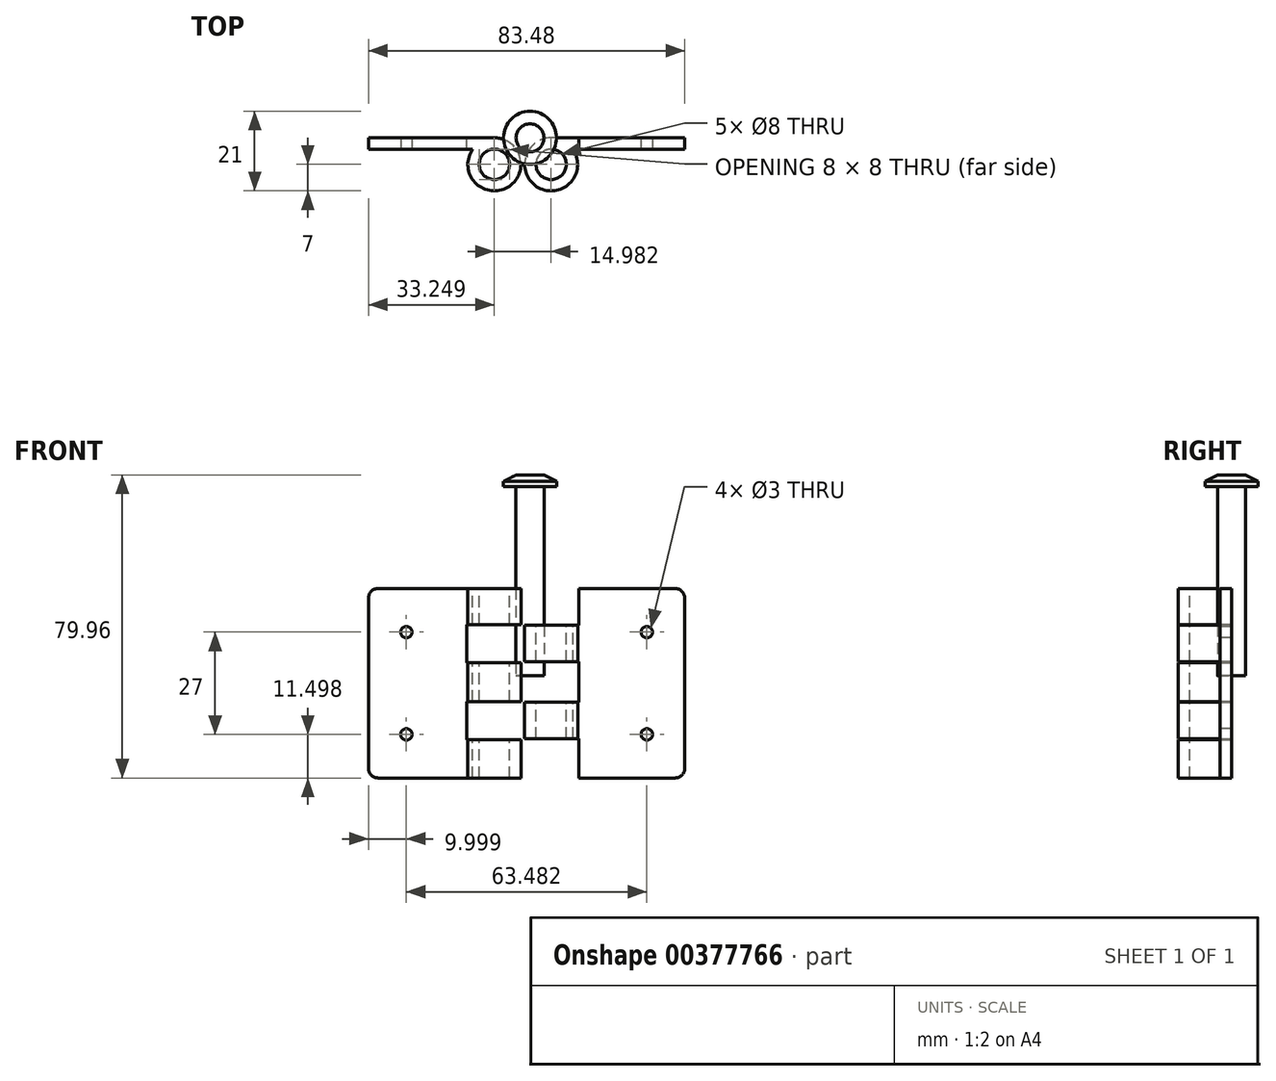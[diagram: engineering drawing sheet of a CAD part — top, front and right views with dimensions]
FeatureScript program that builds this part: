
annotation { "Feature Type Name" : "Feature", "Feature Type Description" : "" }
export const myFeature = defineFeature(function(context is Context, id is Id, definition is map)
    precondition{}
    {
        {
            var Q0;
            Q0=qCreatedBy(makeId("Front.planeOp"),FACE);
            var sketch = newSketch(context, id + "F0", { "sketchPlane" : qUnion([Q0])});
            skLineSegment(sketch, "E0.bottom", {"start": v(-44.61, 37.23) * mm, "end": v(-11.36, 37.23) * mm});
            skLineSegment(sketch, "E0.top", {"start": v(-44.61, -12.77) * mm, "end": v(-11.36, -12.77) * mm});
            skLineSegment(sketch, "E0.left", {"start": v(-44.61, 37.23) * mm, "end": v(-44.61, -12.77) * mm});
            skLineSegment(sketch, "E0.right", {"start": v(-11.36, 37.23) * mm, "end": v(-11.36, -12.77) * mm});
            skSolve(sketch);
        }
        {
            var Q0;
            Q0=qSketchRegion(id+"F0",true);
            extrude(context, id + "F1", {"entities" : qUnion([Q0]), "depth" : 3 * mm});
        }
        {
            var Q0;
            Q0=makeQuery(id+"F1.opExtrude","SWEPT_FACE",FACE,{"disambiguationData":[OSD([sQuery(id+"F0.wireOp",EDGE,"E0.bottom")])]});
            var sketch = newSketch(context, id + "F2", { "sketchPlane" : qUnion([Q0])});
            skCircle(sketch, "E1", {"center": v(-11.36, -7) * mm, "radius": 7 * mm});
            skCircle(sketch, "E2", {"center": v(-11.36, -7) * mm, "radius": 4 * mm});
            skSolve(sketch);
        }
        {
            var Q0;
            {var subQ5=sQuery(id+"F2.wireOp",EDGE,"E2");Q0=makeQuery(id+"F2.imprint","IMPRINT",FACE,{"disambiguationData":[TD([[makeQuery(id+"F2.imprint","IMPRINT",EDGE,{"derivedFrom":subQ5}),-1.0]])]});}
            var Q1;
            {var subQ1=sQuery(id+"F0.wireOp",EDGE,"E0.bottom");var subQ2=makeQuery(id+"F1.opExtrude","SWEPT_EDGE",EDGE,{"disambiguationData":[OSD([subQ1,sQuery(id+"F0.wireOp",EDGE,"E0.right")])]});Q1=makeQuery(id+"F2.imprint","IMPRINT",FACE,{"disambiguationData":[TD([[makeQuery(id+"F2.imprint","IMPRINT",EDGE,{"derivedFrom":subQ2}),1.0]])]});}
            var Q2;
            Q2=makeQuery(id+"F1.opExtrude","SWEPT_FACE",FACE,{"disambiguationData":[OSD([sQuery(id+"F0.wireOp",EDGE,"E0.top")])]});
            extrude(context, id + "F3", {"entities" : qUnion([Q0, Q1]), "operationType" : NewBodyOperationType.ADD, "endBound" : BoundingType.UP_TO_SURFACE, "oppositeDirection" : true, "endBoundEntityFace" : qUnion([Q2]), "depth" : 25.4 * mm});
        }
        {
            var Q0;
            Q0=makeQuery(id+"F1.opExtrude","CAP_FACE",FACE,{"disambiguationData":[OSD([sQuery(id+"F0.wireOp",EDGE,"E0.bottom"),sQuery(id+"F0.wireOp",EDGE,"E0.top"),sQuery(id+"F0.wireOp",EDGE,"E0.left"),sQuery(id+"F0.wireOp",EDGE,"E0.right")])],"isStart":false});
            var sketch = newSketch(context, id + "F4", { "sketchPlane" : qUnion([Q0])});
            skLineSegment(sketch, "E3", {"start": v(-34.61, 37.23) * mm, "end": v(-34.61, -12.77) * mm, "construction": true});
            skCircle(sketch, "E4", {"center": v(-34.61, 25.73) * mm, "radius": 1.5 * mm});
            skCircle(sketch, "E5", {"center": v(-34.61, -1.27) * mm, "radius": 1.5 * mm});
            skSolve(sketch);
        }
        {
            var Q0;
            Q0=makeQuery(id+"F1.opExtrude","SWEPT_EDGE",EDGE,{"disambiguationData":[OSD([sQuery(id+"F0.wireOp",EDGE,"E0.bottom"),sQuery(id+"F0.wireOp",EDGE,"E0.left")])]});
            var Q1;
            Q1=makeQuery(id+"F1.opExtrude","SWEPT_EDGE",EDGE,{"disambiguationData":[OSD([sQuery(id+"F0.wireOp",EDGE,"E0.top"),sQuery(id+"F0.wireOp",EDGE,"E0.left")])]});
            fillet(context, id + "F5", {"entities" : qUnion([Q0, Q1]), "radius" : 2.54 * mm, "tangentPropagation" : true, "allowEdgeOverflow" : false});
        }
        {
            var Q0;
            Q0=makeQuery(id+"F0.imprint","IMPRINT",FACE,{"disambiguationData":[TD([[makeQuery(id+"F0.imprint","IMPRINT",EDGE,{"derivedFrom":sQuery(id+"F0.wireOp",EDGE,"E0.bottom")}),-1.0]])]});
            var sketch = newSketch(context, id + "F6", { "sketchPlane" : qUnion([Q0])});
            skLineSegment(sketch, "E6", {"start": v(-18.61, -2.61) * mm, "end": v(-4.11, -2.61) * mm});
            skLineSegment(sketch, "E7", {"start": v(-4.11, -2.61) * mm, "end": v(-4.11, 7.39) * mm});
            skLineSegment(sketch, "E8", {"start": v(-4.11, 7.39) * mm, "end": v(-18.61, 7.39) * mm});
            skLineSegment(sketch, "E9", {"start": v(-18.61, 7.39) * mm, "end": v(-18.61, -2.61) * mm});
            skLineSegment(sketch, "E10", {"start": v(-18.61, 17.7) * mm, "end": v(-4.11, 17.7) * mm});
            skLineSegment(sketch, "E11", {"start": v(-4.11, 17.7) * mm, "end": v(-4.11, 27.7) * mm});
            skLineSegment(sketch, "E12", {"start": v(-4.11, 27.7) * mm, "end": v(-18.61, 27.7) * mm});
            skLineSegment(sketch, "E13", {"start": v(-18.61, 27.7) * mm, "end": v(-18.61, 17.7) * mm});
            skPoint(sketch, "E14", {"position": v(-11.36, -2.61) * mm});
            skLineSegment(sketch, "E15", {"start": v(-11.36, 27.7) * mm, "end": v(-11.36, 37.23) * mm});
            skLineSegment(sketch, "E16", {"start": v(-11.36, 17.7) * mm, "end": v(-11.36, 7.39) * mm});
            skLineSegment(sketch, "E17", {"start": v(-11.36, -2.61) * mm, "end": v(-11.36, -12.77) * mm});
            skLineSegment(sketch, "E18", {"start": v(-4.11, 17.7) * mm, "end": v(-4.11, 7.39) * mm});
            skLineSegment(sketch, "E19", {"start": v(-18.61, 7.39) * mm, "end": v(-18.61, 17.7) * mm});
            skLineSegment(sketch, "E20", {"start": v(-18.61, 27.7) * mm, "end": v(-18.61, 37.23) * mm});
            skLineSegment(sketch, "E21", {"start": v(-18.61, 37.23) * mm, "end": v(-4.11, 37.23) * mm});
            skLineSegment(sketch, "E22", {"start": v(-4.11, 37.23) * mm, "end": v(-4.11, 27.7) * mm});
            skLineSegment(sketch, "E23", {"start": v(-4.11, -2.61) * mm, "end": v(-4.11, -12.77) * mm});
            skLineSegment(sketch, "E24", {"start": v(-4.11, -12.77) * mm, "end": v(-18.61, -12.77) * mm});
            skLineSegment(sketch, "E25", {"start": v(-18.61, -12.77) * mm, "end": v(-18.61, -2.61) * mm});
            skSolve(sketch);
        }
        {
            var Q0;
            {var subQ0=sQuery(id+"F6.wireOp",EDGE,"E13");Q0=makeQuery(id+"F6.imprint","IMPRINT",FACE,{"disambiguationData":[TD([[makeQuery(id+"F6.imprint","IMPRINT",EDGE,{"derivedFrom":subQ0}),1.0]])]});}
            var Q1;
            {var subQ0=sQuery(id+"F6.wireOp",EDGE,"E11");Q1=makeQuery(id+"F6.imprint","IMPRINT",FACE,{"disambiguationData":[TD([[makeQuery(id+"F6.imprint","IMPRINT",EDGE,{"derivedFrom":subQ0}),1.0]])]});}
            var Q2;
            {var subQ0=sQuery(id+"F6.wireOp",EDGE,"E9");Q2=makeQuery(id+"F6.imprint","IMPRINT",FACE,{"disambiguationData":[TD([[makeQuery(id+"F6.imprint","IMPRINT",EDGE,{"derivedFrom":subQ0}),1.0]])]});}
            var Q3;
            {var subQ0=sQuery(id+"F6.wireOp",EDGE,"E7");Q3=makeQuery(id+"F6.imprint","IMPRINT",FACE,{"disambiguationData":[TD([[makeQuery(id+"F6.imprint","IMPRINT",EDGE,{"derivedFrom":subQ0}),1.0]])]});}
            extrude(context, id + "F7", {"entities" : qUnion([Q0, Q1, Q2, Q3]), "operationType" : NewBodyOperationType.REMOVE, "depth" : 25.4 * mm});
        }
        {
            var Q0;
            Q0=qCreatedBy(makeId("Front.planeOp"),FACE);
            var sketch = newSketch(context, id + "F8", { "sketchPlane" : qUnion([Q0])});
            skLineSegment(sketch, "E26.bottom", {"start": v(3.62, 37.23) * mm, "end": v(38.87, 37.23) * mm});
            skLineSegment(sketch, "E26.top", {"start": v(3.62, -12.77) * mm, "end": v(38.87, -12.77) * mm});
            skLineSegment(sketch, "E26.left", {"start": v(3.62, 37.23) * mm, "end": v(3.62, -12.77) * mm});
            skLineSegment(sketch, "E26.right", {"start": v(38.87, 37.23) * mm, "end": v(38.87, -12.77) * mm});
            skSolve(sketch);
        }
        {
            var Q0;
            Q0=qSketchRegion(id+"F8",true);
            extrude(context, id + "F9", {"entities" : qUnion([Q0]), "depth" : 3 * mm});
        }
        {
            var Q0;
            Q0=makeQuery(id+"F9.opExtrude","SWEPT_FACE",FACE,{"disambiguationData":[OSD([sQuery(id+"F8.wireOp",EDGE,"E26.bottom")])]});
            var sketch = newSketch(context, id + "F10", { "sketchPlane" : qUnion([Q0])});
            skCircle(sketch, "E27", {"center": v(3.62, -7) * mm, "radius": 7 * mm});
            skLineSegment(sketch, "E28", {"start": v(-33.9, -7) * mm, "end": v(23.07, -7) * mm, "construction": true});
            skCircle(sketch, "E29", {"center": v(3.62, -7) * mm, "radius": 4 * mm});
            skSolve(sketch);
        }
        {
            var Q0;
            {var subQ5=sQuery(id+"F10.wireOp",EDGE,"E29");Q0=makeQuery(id+"F10.imprint","IMPRINT",FACE,{"disambiguationData":[TD([[makeQuery(id+"F10.imprint","IMPRINT",EDGE,{"derivedFrom":subQ5}),-1.0]])]});}
            var Q1;
            {var subQ1=sQuery(id+"F8.wireOp",EDGE,"E26.bottom");var subQ2=makeQuery(id+"F9.opExtrude","SWEPT_EDGE",EDGE,{"disambiguationData":[OSD([subQ1,sQuery(id+"F8.wireOp",EDGE,"E26.left")])]});Q1=makeQuery(id+"F10.imprint","IMPRINT",FACE,{"disambiguationData":[TD([[makeQuery(id+"F10.imprint","IMPRINT",EDGE,{"derivedFrom":subQ2}),-1.0]])]});}
            var Q2;
            Q2=makeQuery(id+"F9.opExtrude","SWEPT_FACE",FACE,{"disambiguationData":[OSD([sQuery(id+"F8.wireOp",EDGE,"E26.top")])]});
            extrude(context, id + "F11", {"entities" : qUnion([Q0, Q1]), "operationType" : NewBodyOperationType.ADD, "endBound" : BoundingType.UP_TO_SURFACE, "oppositeDirection" : true, "endBoundEntityFace" : qUnion([Q2]), "depth" : 25.4 * mm});
        }
        {
            var Q0;
            Q0=makeQuery(id+"F9.opExtrude","CAP_FACE",FACE,{"disambiguationData":[OSD([sQuery(id+"F8.wireOp",EDGE,"E26.bottom"),sQuery(id+"F8.wireOp",EDGE,"E26.top"),sQuery(id+"F8.wireOp",EDGE,"E26.left"),sQuery(id+"F8.wireOp",EDGE,"E26.right")])],"isStart":true});
            var sketch = newSketch(context, id + "F12", { "sketchPlane" : qUnion([Q0])});
            skLineSegment(sketch, "E30", {"start": v(-10.87, 27.5) * mm, "end": v(3.63, 27.5) * mm});
            skLineSegment(sketch, "E31", {"start": v(3.63, 27.5) * mm, "end": v(3.63, 37.23) * mm});
            skLineSegment(sketch, "E32", {"start": v(3.63, 37.23) * mm, "end": v(-10.87, 37.23) * mm});
            skLineSegment(sketch, "E33", {"start": v(-10.87, 27.5) * mm, "end": v(-10.87, 37.23) * mm});
            skLineSegment(sketch, "E34", {"start": v(-10.87, 27.5) * mm, "end": v(-10.87, -12.77) * mm});
            skLineSegment(sketch, "E35", {"start": v(-10.87, -12.77) * mm, "end": v(3.63, -12.77) * mm});
            skLineSegment(sketch, "E36", {"start": v(3.63, -12.77) * mm, "end": v(3.63, 27.5) * mm});
            skLineSegment(sketch, "E37", {"start": v(3.63, 17.9) * mm, "end": v(-10.87, 17.9) * mm});
            skLineSegment(sketch, "E38", {"start": v(-10.87, 7.19) * mm, "end": v(3.63, 7.19) * mm});
            skLineSegment(sketch, "E39", {"start": v(-10.87, -2.41) * mm, "end": v(3.63, -2.41) * mm});
            skSolve(sketch);
        }
        {
            var Q0;
            {var subQ0=sQuery(id+"F12.wireOp",EDGE,"E31");Q0=makeQuery(id+"F12.imprint","IMPRINT",FACE,{"disambiguationData":[TD([[makeQuery(id+"F12.imprint","IMPRINT",EDGE,{"derivedFrom":subQ0}),1.0]])]});}
            var Q1;
            {var subQ0=sQuery(id+"F12.wireOp",EDGE,"E33");Q1=makeQuery(id+"F12.imprint","IMPRINT",FACE,{"disambiguationData":[TD([[makeQuery(id+"F12.imprint","IMPRINT",EDGE,{"derivedFrom":subQ0}),-1.0]])]});}
            var Q2;
            {var subQ0=sQuery(id+"F12.wireOp",EDGE,"E37");var subQ1=sQuery(id+"F12.wireOp",EDGE,"E34");var subQ2=makeQuery(id+"F12.imprint","INTERSECT",VERTEX,{"derivedFrom":[subQ1,subQ0]});Q2=makeQuery(id+"F12.imprint","IMPRINT",FACE,{"disambiguationData":[TD([[makeQuery(id+"F12.imprint","IMPRINT",EDGE,{"disambiguationData":[TD([[subQ2,-1.0]])],"derivedFrom":subQ1}),1.0]])]});}
            var Q3;
            {var subQ0=sQuery(id+"F12.wireOp",EDGE,"E37");var subQ1=sQuery(id+"F12.wireOp",EDGE,"E36");var subQ2=makeQuery(id+"F12.imprint","INTERSECT",VERTEX,{"derivedFrom":[subQ1,subQ0]});Q3=makeQuery(id+"F12.imprint","IMPRINT",FACE,{"disambiguationData":[TD([[makeQuery(id+"F12.imprint","IMPRINT",EDGE,{"disambiguationData":[TD([[subQ2,1.0]])],"derivedFrom":subQ1}),1.0]])]});}
            var Q4;
            {var subQ0=sQuery(id+"F12.wireOp",EDGE,"E35");var subQ3=sQuery(id+"F12.wireOp",EDGE,"E36");var subQ4=makeQuery(id+"F12.imprint","INTERSECT",VERTEX,{"derivedFrom":[subQ0,subQ3]});Q4=makeQuery(id+"F12.imprint","IMPRINT",FACE,{"disambiguationData":[TD([[makeQuery(id+"F12.imprint","IMPRINT",EDGE,{"disambiguationData":[TD([[subQ4,1.0]])],"derivedFrom":subQ0}),1.0]])]});}
            var Q5;
            {var subQ1=sQuery(id+"F12.wireOp",EDGE,"E34");var subQ3=sQuery(id+"F12.wireOp",EDGE,"E39");var subQ4=makeQuery(id+"F12.imprint","INTERSECT",VERTEX,{"derivedFrom":[subQ1,subQ3]});Q5=makeQuery(id+"F12.imprint","IMPRINT",FACE,{"disambiguationData":[TD([[makeQuery(id+"F12.imprint","IMPRINT",EDGE,{"disambiguationData":[TD([[subQ4,-1.0]])],"derivedFrom":subQ3}),-1.0]])]});}
            extrude(context, id + "F13", {"entities" : qUnion([Q0, Q1, Q2, Q3, Q4, Q5]), "operationType" : NewBodyOperationType.REMOVE, "oppositeDirection" : true, "depth" : 25.4 * mm});
        }
        {
            var Q0;
            Q0=qCreatedBy(makeId("Front.planeOp"),FACE);
            var sketch = newSketch(context, id + "F14", { "sketchPlane" : qUnion([Q0])});
            skLineSegment(sketch, "E40", {"start": v(-5.66, 64.2) * mm, "end": v(-5.66, 14.2) * mm});
            skLineSegment(sketch, "E41", {"start": v(-5.66, 14.2) * mm, "end": v(-1.96, 14.2) * mm});
            skLineSegment(sketch, "E42", {"start": v(-1.96, 14.2) * mm, "end": v(-1.96, 67.2) * mm});
            skLineSegment(sketch, "E43", {"start": v(-1.96, 67.2) * mm, "end": v(-5.66, 67.2) * mm});
            skLineSegment(sketch, "E44", {"start": v(-5.66, 67.2) * mm, "end": v(-8.96, 65.52) * mm});
            skLineSegment(sketch, "E45", {"start": v(-8.96, 65.52) * mm, "end": v(-8.96, 64.2) * mm});
            skLineSegment(sketch, "E46", {"start": v(-8.96, 64.2) * mm, "end": v(-5.66, 64.2) * mm});
            skSolve(sketch);
        }
        {
            var Q0;
            Q0=qSketchRegion(id+"F14",true);
            var Q1;
            Q1=sQuery(id+"F14.wireOp",EDGE,"E42");
            revolve(context, id + "F15", {"entities" : qUnion([Q0]), "axis" : qUnion([Q1]), "revolveType" : RevolveType.FULL});
        }
        {
            var Q0;
            Q0=makeQuery(id+"F9.opExtrude","CAP_FACE",FACE,{"disambiguationData":[OSD([sQuery(id+"F8.wireOp",EDGE,"E26.bottom"),sQuery(id+"F8.wireOp",EDGE,"E26.top"),sQuery(id+"F8.wireOp",EDGE,"E26.left"),sQuery(id+"F8.wireOp",EDGE,"E26.right")])],"isStart":false});
            var sketch = newSketch(context, id + "F16", { "sketchPlane" : qUnion([Q0])});
            skLineSegment(sketch, "E47", {"start": v(28.87, 37.23) * mm, "end": v(28.87, -12.77) * mm, "construction": true});
            skCircle(sketch, "E48", {"center": v(28.87, 25.73) * mm, "radius": 1.5 * mm});
            skCircle(sketch, "E49", {"center": v(28.87, -1.27) * mm, "radius": 1.5 * mm});
            skSolve(sketch);
        }
        {
            var Q0;
            Q0=makeQuery(id+"F9.opExtrude","SWEPT_EDGE",EDGE,{"disambiguationData":[OSD([sQuery(id+"F8.wireOp",EDGE,"E26.bottom"),sQuery(id+"F8.wireOp",EDGE,"E26.right")])]});
            var Q1;
            Q1=makeQuery(id+"F9.opExtrude","SWEPT_EDGE",EDGE,{"disambiguationData":[OSD([sQuery(id+"F8.wireOp",EDGE,"E26.top"),sQuery(id+"F8.wireOp",EDGE,"E26.right")])]});
            fillet(context, id + "F17", {"entities" : qUnion([Q0, Q1]), "radius" : 2.54 * mm, "tangentPropagation" : true, "allowEdgeOverflow" : false});
        }
        {
            var Q0;
            Q0=makeQuery(id+"F4.imprint","IMPRINT",FACE,{"disambiguationData":[TD([[makeQuery(id+"F4.imprint","IMPRINT",EDGE,{"derivedFrom":sQuery(id+"F4.wireOp",EDGE,"E5")}),1.0]])]});
            var Q1;
            Q1=makeQuery(id+"F4.imprint","IMPRINT",FACE,{"disambiguationData":[TD([[makeQuery(id+"F4.imprint","IMPRINT",EDGE,{"derivedFrom":sQuery(id+"F4.wireOp",EDGE,"E4")}),1.0]])]});
            extrude(context, id + "F18", {"entities" : qUnion([Q0, Q1]), "operationType" : NewBodyOperationType.REMOVE, "oppositeDirection" : true, "depth" : 3 * mm});
        }
        {
            var Q0;
            Q0 = qSketchRegion(id + "F16", true);
            extrude(context, id + "F19", {"entities" : qUnion([Q0]), "operationType" : NewBodyOperationType.REMOVE, "oppositeDirection" : true, "depth" : 3 * mm});
        }
    });
